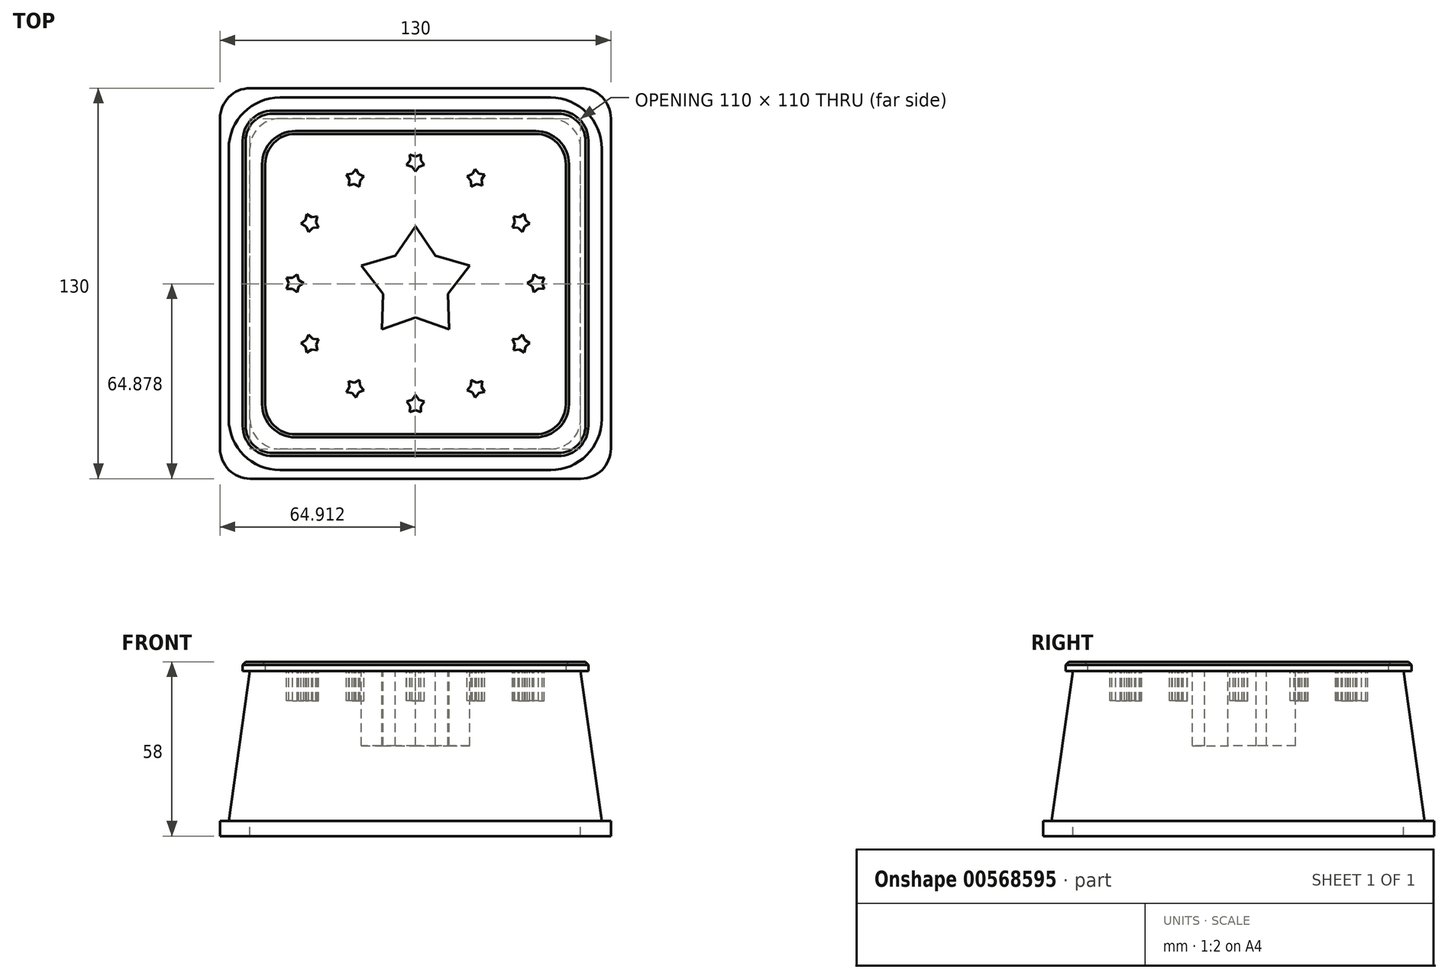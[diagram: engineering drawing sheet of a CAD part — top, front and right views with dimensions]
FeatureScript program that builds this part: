
annotation { "Feature Type Name" : "Feature", "Feature Type Description" : "" }
export const myFeature = defineFeature(function(context is Context, id is Id, definition is map)
    precondition{}
    {
        {
            var Q0;
            Q0=qCreatedBy(makeId("Top.planeOp"),FACE);
            var sketch = newSketch(context, id + "F0", { "sketchPlane" : qUnion([Q0])});
            skLineSegment(sketch, "E0", {"start": v(6.68, 9.2) * mm, "end": v(0, 18.96) * mm});
            skPoint(sketch, "E1.middle", {"position": v(0, 0) * mm});
            skPoint(sketch, "E2.visualSharp", {"position": v(-40, 40) * mm});
            skPoint(sketch, "E3.visualSharp", {"position": v(40, 40) * mm});
            skPoint(sketch, "E4.visualSharp", {"position": v(40, -40) * mm});
            skPoint(sketch, "E5.visualSharp", {"position": v(-40, -40) * mm});
            skLineSegment(sketch, "E6.bottom", {"start": v(40, -50.28) * mm, "end": v(-40, -50.28) * mm});
            skLineSegment(sketch, "E6.top", {"start": v(40, 49.72) * mm, "end": v(-40, 49.72) * mm});
            skLineSegment(sketch, "E6.left", {"start": v(50, -40.28) * mm, "end": v(50, 39.72) * mm});
            skLineSegment(sketch, "E6.right", {"start": v(-50, -40.28) * mm, "end": v(-50, 39.72) * mm});
            skArc(sketch, "E7.filletArc", {"start": v(-40, 49.72) * mm, "mid": v(-47.06, 46.79) * mm, "end": v(-50, 39.72) * mm});
            skArc(sketch, "E8.filletArc", {"start": v(50, 39.72) * mm, "mid": v(47.08, 46.79) * mm, "end": v(40, 49.72) * mm});
            skArc(sketch, "E9.filletArc", {"start": v(40, -50.28) * mm, "mid": v(47.08, -47.35) * mm, "end": v(50, -40.28) * mm});
            skArc(sketch, "E10.filletArc", {"start": v(-50, -40.28) * mm, "mid": v(-47.06, -47.35) * mm, "end": v(-40, -50.28) * mm});
            skLineSegment(sketch, "E11.bottom", {"start": v(44.91, -55.17) * mm, "end": v(-45.09, -55.17) * mm});
            skLineSegment(sketch, "E11.top", {"start": v(44.91, 54.83) * mm, "end": v(-45.09, 54.83) * mm});
            skLineSegment(sketch, "E11.left", {"start": v(54.91, -45.17) * mm, "end": v(54.91, 44.83) * mm});
            skLineSegment(sketch, "E11.right", {"start": v(-55.09, -45.17) * mm, "end": v(-55.09, 44.83) * mm});
            skArc(sketch, "E12.filletArc", {"start": v(-45.09, 54.83) * mm, "mid": v(-52.16, 51.9) * mm, "end": v(-55.09, 44.83) * mm});
            skArc(sketch, "E13.filletArc", {"start": v(54.91, 44.83) * mm, "mid": v(51.98, 51.9) * mm, "end": v(44.91, 54.83) * mm});
            skArc(sketch, "E14.filletArc", {"start": v(44.91, -55.17) * mm, "mid": v(51.98, -52.24) * mm, "end": v(54.91, -45.17) * mm});
            skArc(sketch, "E15.filletArc", {"start": v(-55.09, -45.17) * mm, "mid": v(-52.16, -52.24) * mm, "end": v(-45.09, -55.17) * mm});
            skLineSegment(sketch, "E16.bottom", {"start": v(47.51, -57.5) * mm, "end": v(-47.49, -57.5) * mm});
            skLineSegment(sketch, "E16.top", {"start": v(47.51, 57.5) * mm, "end": v(-47.49, 57.5) * mm});
            skLineSegment(sketch, "E16.left", {"start": v(57.51, -47.5) * mm, "end": v(57.51, 47.5) * mm});
            skLineSegment(sketch, "E16.right", {"start": v(-57.49, -47.5) * mm, "end": v(-57.49, 47.5) * mm});
            skArc(sketch, "E17.filletArc", {"start": v(-47.49, 57.5) * mm, "mid": v(-54.56, 54.56) * mm, "end": v(-57.49, 47.5) * mm});
            skArc(sketch, "E18.filletArc", {"start": v(57.51, 47.5) * mm, "mid": v(54.58, 54.56) * mm, "end": v(47.51, 57.5) * mm});
            skArc(sketch, "E19.filletArc", {"start": v(47.51, -57.5) * mm, "mid": v(54.58, -54.58) * mm, "end": v(57.51, -47.5) * mm});
            skArc(sketch, "E20.filletArc", {"start": v(-57.49, -47.5) * mm, "mid": v(-54.56, -54.58) * mm, "end": v(-47.49, -57.5) * mm});
            skLineSegment(sketch, "E21.bottom", {"start": v(55, -65.05) * mm, "end": v(-55, -65.05) * mm});
            skLineSegment(sketch, "E21.top", {"start": v(55, 64.95) * mm, "end": v(-55, 64.95) * mm});
            skLineSegment(sketch, "E21.left", {"start": v(65, -55.05) * mm, "end": v(65, 54.95) * mm});
            skLineSegment(sketch, "E21.right", {"start": v(-65, -55.05) * mm, "end": v(-65, 54.95) * mm});
            skArc(sketch, "E22.filletArc", {"start": v(-55, 64.95) * mm, "mid": v(-62.07, 62.02) * mm, "end": v(-65, 54.95) * mm});
            skArc(sketch, "E23.filletArc", {"start": v(65, 54.95) * mm, "mid": v(62.07, 62.02) * mm, "end": v(55, 64.95) * mm});
            skArc(sketch, "E24.filletArc", {"start": v(55, -65.05) * mm, "mid": v(62.07, -62.12) * mm, "end": v(65, -55.05) * mm});
            skArc(sketch, "E25.filletArc", {"start": v(-65, -55.05) * mm, "mid": v(-62.07, -62.12) * mm, "end": v(-55, -65.05) * mm});
            skLineSegment(sketch, "E26", {"start": v(-18.04, 5.85) * mm, "end": v(-10.83, -3.53) * mm});
            skLineSegment(sketch, "E27", {"start": v(-10.83, -3.53) * mm, "end": v(-11.15, -15.35) * mm});
            skLineSegment(sketch, "E28", {"start": v(-11.15, -15.35) * mm, "end": v(0, -11.39) * mm});
            skLineSegment(sketch, "E29", {"start": v(0, -11.39) * mm, "end": v(11.13, -15.35) * mm});
            skLineSegment(sketch, "E30", {"start": v(11.13, -15.35) * mm, "end": v(10.8, -3.53) * mm});
            skLineSegment(sketch, "E31", {"start": v(10.8, -3.53) * mm, "end": v(18.02, 5.85) * mm});
            skLineSegment(sketch, "E32", {"start": v(18.02, 5.85) * mm, "end": v(6.68, 9.19) * mm});
            skLineSegment(sketch, "E33", {"start": v(6.68, 9.19) * mm, "end": v(0, 18.94) * mm});
            skLineSegment(sketch, "E34", {"start": v(0, 18.94) * mm, "end": v(-6.7, 9.19) * mm});
            skLineSegment(sketch, "E35", {"start": v(-6.7, 9.19) * mm, "end": v(-18.04, 5.85) * mm});
            skPoint(sketch, "E36.middle", {"position": v(0, -0.01) * mm});
            skLineSegment(sketch, "E37", {"start": v(0, -42.21) * mm, "end": v(1.85, -42.87) * mm});
            skLineSegment(sketch, "E38", {"start": v(1.8, -40.92) * mm, "end": v(2.98, -39.37) * mm});
            skLineSegment(sketch, "E39", {"start": v(1.11, -38.82) * mm, "end": v(0, -37.21) * mm});
            skLineSegment(sketch, "E40", {"start": v(-1.1, -38.82) * mm, "end": v(-2.96, -39.37) * mm});
            skPoint(sketch, "E41.middle", {"position": v(0, -40.34) * mm});
            skLineSegment(sketch, "E42", {"start": v(-1.78, -40.92) * mm, "end": v(-1.83, -42.87) * mm});
            skLineSegment(sketch, "E43", {"start": v(1.8, -40.92) * mm, "end": v(1.85, -42.87) * mm});
            skLineSegment(sketch, "E44", {"start": v(0, -42.21) * mm, "end": v(-1.83, -42.87) * mm});
            skLineSegment(sketch, "E45", {"start": v(-1.78, -40.92) * mm, "end": v(-2.96, -39.37) * mm});
            skLineSegment(sketch, "E46", {"start": v(-1.1, -38.82) * mm, "end": v(0, -37.21) * mm});
            skLineSegment(sketch, "E47", {"start": v(1.11, -38.82) * mm, "end": v(2.98, -39.37) * mm});
            skLineSegment(sketch, "E48.1.0", {"start": v(18.92, -36.33) * mm, "end": v(17.12, -35.58) * mm});
            skLineSegment(sketch, "E48.1.1", {"start": v(18.92, -36.33) * mm, "end": v(19.85, -38.04) * mm});
            skLineSegment(sketch, "E48.1.2", {"start": v(21.11, -36.55) * mm, "end": v(19.85, -38.04) * mm});
            skLineSegment(sketch, "E48.1.3", {"start": v(22.01, -34.54) * mm, "end": v(22.27, -32.6) * mm});
            skLineSegment(sketch, "E48.1.4", {"start": v(20.37, -33.07) * mm, "end": v(22.27, -32.6) * mm});
            skPoint(sketch, "E48.1.5", {"position": v(20.18, -34.93) * mm});
            skLineSegment(sketch, "E48.1.6", {"start": v(18.46, -34.17) * mm, "end": v(17.12, -35.58) * mm});
            skLineSegment(sketch, "E48.1.7", {"start": v(22.01, -34.54) * mm, "end": v(23.03, -36.2) * mm});
            skLineSegment(sketch, "E48.1.8", {"start": v(18.46, -34.17) * mm, "end": v(18.61, -32.22) * mm});
            skLineSegment(sketch, "E48.1.9", {"start": v(20.37, -33.07) * mm, "end": v(18.61, -32.22) * mm});
            skLineSegment(sketch, "E48.1.10", {"start": v(21.11, -36.55) * mm, "end": v(23.03, -36.2) * mm});
            skPoint(sketch, "E48.1.11", {"position": v(20.18, -34.93) * mm});
            skLineSegment(sketch, "E48.2.0", {"start": v(34.55, -22) * mm, "end": v(32.62, -22.25) * mm});
            skLineSegment(sketch, "E48.2.1", {"start": v(34.55, -22) * mm, "end": v(36.21, -23.02) * mm});
            skLineSegment(sketch, "E48.2.2", {"start": v(36.56, -21.1) * mm, "end": v(36.21, -23.02) * mm});
            skLineSegment(sketch, "E48.2.3", {"start": v(36.33, -18.9) * mm, "end": v(35.59, -17.1) * mm});
            skLineSegment(sketch, "E48.2.4", {"start": v(34.18, -18.45) * mm, "end": v(35.59, -17.1) * mm});
            skPoint(sketch, "E48.2.5", {"position": v(34.94, -20.16) * mm});
            skLineSegment(sketch, "E48.2.6", {"start": v(33.07, -20.36) * mm, "end": v(32.62, -22.25) * mm});
            skLineSegment(sketch, "E48.2.7", {"start": v(36.33, -18.9) * mm, "end": v(38.05, -19.84) * mm});
            skLineSegment(sketch, "E48.2.8", {"start": v(33.07, -20.36) * mm, "end": v(32.23, -18.6) * mm});
            skLineSegment(sketch, "E48.2.9", {"start": v(34.18, -18.45) * mm, "end": v(32.23, -18.6) * mm});
            skLineSegment(sketch, "E48.2.10", {"start": v(36.56, -21.1) * mm, "end": v(38.05, -19.84) * mm});
            skPoint(sketch, "E48.2.11", {"position": v(34.94, -20.16) * mm});
            skLineSegment(sketch, "E48.3.0", {"start": v(40.92, -1.78) * mm, "end": v(39.37, -2.96) * mm});
            skLineSegment(sketch, "E48.3.1", {"start": v(40.92, -1.78) * mm, "end": v(42.87, -1.83) * mm});
            skLineSegment(sketch, "E48.3.2", {"start": v(42.21, 0) * mm, "end": v(42.87, -1.83) * mm});
            skLineSegment(sketch, "E48.3.3", {"start": v(40.92, 1.8) * mm, "end": v(39.37, 2.98) * mm});
            skLineSegment(sketch, "E48.3.4", {"start": v(38.82, 1.11) * mm, "end": v(39.37, 2.98) * mm});
            skPoint(sketch, "E48.3.5", {"position": v(40.34, 0) * mm});
            skLineSegment(sketch, "E48.3.6", {"start": v(38.82, -1.1) * mm, "end": v(39.37, -2.96) * mm});
            skLineSegment(sketch, "E48.3.7", {"start": v(40.92, 1.8) * mm, "end": v(42.87, 1.85) * mm});
            skLineSegment(sketch, "E48.3.8", {"start": v(38.82, -1.1) * mm, "end": v(37.21, 0) * mm});
            skLineSegment(sketch, "E48.3.9", {"start": v(38.82, 1.11) * mm, "end": v(37.21, 0) * mm});
            skLineSegment(sketch, "E48.3.10", {"start": v(42.21, 0) * mm, "end": v(42.87, 1.85) * mm});
            skPoint(sketch, "E48.3.11", {"position": v(40.34, 0) * mm});
            skLineSegment(sketch, "E48.4.0", {"start": v(36.33, 18.92) * mm, "end": v(35.58, 17.12) * mm});
            skLineSegment(sketch, "E48.4.1", {"start": v(36.33, 18.92) * mm, "end": v(38.04, 19.85) * mm});
            skLineSegment(sketch, "E48.4.2", {"start": v(36.55, 21.11) * mm, "end": v(38.04, 19.85) * mm});
            skLineSegment(sketch, "E48.4.3", {"start": v(34.54, 22.01) * mm, "end": v(32.6, 22.27) * mm});
            skLineSegment(sketch, "E48.4.4", {"start": v(33.07, 20.37) * mm, "end": v(32.6, 22.27) * mm});
            skPoint(sketch, "E48.4.5", {"position": v(34.93, 20.18) * mm});
            skLineSegment(sketch, "E48.4.6", {"start": v(34.17, 18.46) * mm, "end": v(35.58, 17.12) * mm});
            skLineSegment(sketch, "E48.4.7", {"start": v(34.54, 22.01) * mm, "end": v(36.2, 23.03) * mm});
            skLineSegment(sketch, "E48.4.8", {"start": v(34.17, 18.46) * mm, "end": v(32.22, 18.61) * mm});
            skLineSegment(sketch, "E48.4.9", {"start": v(33.07, 20.37) * mm, "end": v(32.22, 18.61) * mm});
            skLineSegment(sketch, "E48.4.10", {"start": v(36.55, 21.11) * mm, "end": v(36.2, 23.03) * mm});
            skPoint(sketch, "E48.4.11", {"position": v(34.93, 20.18) * mm});
            skLineSegment(sketch, "E48.5.0", {"start": v(22, 34.55) * mm, "end": v(22.25, 32.62) * mm});
            skLineSegment(sketch, "E48.5.1", {"start": v(22, 34.55) * mm, "end": v(23.02, 36.21) * mm});
            skLineSegment(sketch, "E48.5.2", {"start": v(21.1, 36.56) * mm, "end": v(23.02, 36.21) * mm});
            skLineSegment(sketch, "E48.5.3", {"start": v(18.9, 36.33) * mm, "end": v(17.1, 35.59) * mm});
            skLineSegment(sketch, "E48.5.4", {"start": v(18.45, 34.18) * mm, "end": v(17.1, 35.59) * mm});
            skPoint(sketch, "E48.5.5", {"position": v(20.16, 34.94) * mm});
            skLineSegment(sketch, "E48.5.6", {"start": v(20.36, 33.07) * mm, "end": v(22.25, 32.62) * mm});
            skLineSegment(sketch, "E48.5.7", {"start": v(18.9, 36.33) * mm, "end": v(19.84, 38.05) * mm});
            skLineSegment(sketch, "E48.5.8", {"start": v(20.36, 33.07) * mm, "end": v(18.6, 32.23) * mm});
            skLineSegment(sketch, "E48.5.9", {"start": v(18.45, 34.18) * mm, "end": v(18.6, 32.23) * mm});
            skLineSegment(sketch, "E48.5.10", {"start": v(21.1, 36.56) * mm, "end": v(19.84, 38.05) * mm});
            skPoint(sketch, "E48.5.11", {"position": v(20.16, 34.94) * mm});
            skLineSegment(sketch, "E48.6.0", {"start": v(1.78, 40.92) * mm, "end": v(2.96, 39.37) * mm});
            skLineSegment(sketch, "E48.6.1", {"start": v(1.78, 40.92) * mm, "end": v(1.83, 42.87) * mm});
            skLineSegment(sketch, "E48.6.2", {"start": v(0, 42.21) * mm, "end": v(1.83, 42.87) * mm});
            skLineSegment(sketch, "E48.6.3", {"start": v(-1.8, 40.92) * mm, "end": v(-2.98, 39.37) * mm});
            skLineSegment(sketch, "E48.6.4", {"start": v(-1.11, 38.82) * mm, "end": v(-2.98, 39.37) * mm});
            skPoint(sketch, "E48.6.5", {"position": v(0, 40.34) * mm});
            skLineSegment(sketch, "E48.6.6", {"start": v(1.1, 38.82) * mm, "end": v(2.96, 39.37) * mm});
            skLineSegment(sketch, "E48.6.7", {"start": v(-1.8, 40.92) * mm, "end": v(-1.85, 42.87) * mm});
            skLineSegment(sketch, "E48.6.8", {"start": v(1.1, 38.82) * mm, "end": v(0, 37.21) * mm});
            skLineSegment(sketch, "E48.6.9", {"start": v(-1.11, 38.82) * mm, "end": v(0, 37.21) * mm});
            skLineSegment(sketch, "E48.6.10", {"start": v(0, 42.21) * mm, "end": v(-1.85, 42.87) * mm});
            skPoint(sketch, "E48.6.11", {"position": v(0, 40.34) * mm});
            skLineSegment(sketch, "E48.7.0", {"start": v(-18.92, 36.33) * mm, "end": v(-17.12, 35.58) * mm});
            skLineSegment(sketch, "E48.7.1", {"start": v(-18.92, 36.33) * mm, "end": v(-19.85, 38.04) * mm});
            skLineSegment(sketch, "E48.7.2", {"start": v(-21.11, 36.55) * mm, "end": v(-19.85, 38.04) * mm});
            skLineSegment(sketch, "E48.7.3", {"start": v(-22.01, 34.54) * mm, "end": v(-22.27, 32.6) * mm});
            skLineSegment(sketch, "E48.7.4", {"start": v(-20.37, 33.07) * mm, "end": v(-22.27, 32.6) * mm});
            skPoint(sketch, "E48.7.5", {"position": v(-20.18, 34.93) * mm});
            skLineSegment(sketch, "E48.7.6", {"start": v(-18.46, 34.17) * mm, "end": v(-17.12, 35.58) * mm});
            skLineSegment(sketch, "E48.7.7", {"start": v(-22.01, 34.54) * mm, "end": v(-23.03, 36.2) * mm});
            skLineSegment(sketch, "E48.7.8", {"start": v(-18.46, 34.17) * mm, "end": v(-18.61, 32.22) * mm});
            skLineSegment(sketch, "E48.7.9", {"start": v(-20.37, 33.07) * mm, "end": v(-18.61, 32.22) * mm});
            skLineSegment(sketch, "E48.7.10", {"start": v(-21.11, 36.55) * mm, "end": v(-23.03, 36.2) * mm});
            skPoint(sketch, "E48.7.11", {"position": v(-20.18, 34.93) * mm});
            skLineSegment(sketch, "E48.8.0", {"start": v(-34.55, 22) * mm, "end": v(-32.62, 22.25) * mm});
            skLineSegment(sketch, "E48.8.1", {"start": v(-34.55, 22) * mm, "end": v(-36.21, 23.02) * mm});
            skLineSegment(sketch, "E48.8.2", {"start": v(-36.56, 21.1) * mm, "end": v(-36.21, 23.02) * mm});
            skLineSegment(sketch, "E48.8.3", {"start": v(-36.33, 18.9) * mm, "end": v(-35.59, 17.1) * mm});
            skLineSegment(sketch, "E48.8.4", {"start": v(-34.18, 18.45) * mm, "end": v(-35.59, 17.1) * mm});
            skPoint(sketch, "E48.8.5", {"position": v(-34.94, 20.16) * mm});
            skLineSegment(sketch, "E48.8.6", {"start": v(-33.07, 20.36) * mm, "end": v(-32.62, 22.25) * mm});
            skLineSegment(sketch, "E48.8.7", {"start": v(-36.33, 18.9) * mm, "end": v(-38.05, 19.84) * mm});
            skLineSegment(sketch, "E48.8.8", {"start": v(-33.07, 20.36) * mm, "end": v(-32.23, 18.6) * mm});
            skLineSegment(sketch, "E48.8.9", {"start": v(-34.18, 18.45) * mm, "end": v(-32.23, 18.6) * mm});
            skLineSegment(sketch, "E48.8.10", {"start": v(-36.56, 21.1) * mm, "end": v(-38.05, 19.84) * mm});
            skPoint(sketch, "E48.8.11", {"position": v(-34.94, 20.16) * mm});
            skLineSegment(sketch, "E48.9.0", {"start": v(-40.92, 1.78) * mm, "end": v(-39.37, 2.96) * mm});
            skLineSegment(sketch, "E48.9.1", {"start": v(-40.92, 1.78) * mm, "end": v(-42.87, 1.83) * mm});
            skLineSegment(sketch, "E48.9.2", {"start": v(-42.21, 0) * mm, "end": v(-42.87, 1.83) * mm});
            skLineSegment(sketch, "E48.9.3", {"start": v(-40.92, -1.8) * mm, "end": v(-39.37, -2.98) * mm});
            skLineSegment(sketch, "E48.9.4", {"start": v(-38.82, -1.11) * mm, "end": v(-39.37, -2.98) * mm});
            skPoint(sketch, "E48.9.5", {"position": v(-40.34, 0) * mm});
            skLineSegment(sketch, "E48.9.6", {"start": v(-38.82, 1.1) * mm, "end": v(-39.37, 2.96) * mm});
            skLineSegment(sketch, "E48.9.7", {"start": v(-40.92, -1.8) * mm, "end": v(-42.87, -1.85) * mm});
            skLineSegment(sketch, "E48.9.8", {"start": v(-38.82, 1.1) * mm, "end": v(-37.21, 0) * mm});
            skLineSegment(sketch, "E48.9.9", {"start": v(-38.82, -1.11) * mm, "end": v(-37.21, 0) * mm});
            skLineSegment(sketch, "E48.9.10", {"start": v(-42.21, 0) * mm, "end": v(-42.87, -1.85) * mm});
            skPoint(sketch, "E48.9.11", {"position": v(-40.34, 0) * mm});
            skLineSegment(sketch, "E48.10.0", {"start": v(-36.33, -18.92) * mm, "end": v(-35.58, -17.12) * mm});
            skLineSegment(sketch, "E48.10.1", {"start": v(-36.33, -18.92) * mm, "end": v(-38.04, -19.85) * mm});
            skLineSegment(sketch, "E48.10.2", {"start": v(-36.55, -21.11) * mm, "end": v(-38.04, -19.85) * mm});
            skLineSegment(sketch, "E48.10.3", {"start": v(-34.54, -22.01) * mm, "end": v(-32.6, -22.27) * mm});
            skLineSegment(sketch, "E48.10.4", {"start": v(-33.07, -20.37) * mm, "end": v(-32.6, -22.27) * mm});
            skPoint(sketch, "E48.10.5", {"position": v(-34.93, -20.18) * mm});
            skLineSegment(sketch, "E48.10.6", {"start": v(-34.17, -18.46) * mm, "end": v(-35.58, -17.12) * mm});
            skLineSegment(sketch, "E48.10.7", {"start": v(-34.54, -22.01) * mm, "end": v(-36.2, -23.03) * mm});
            skLineSegment(sketch, "E48.10.8", {"start": v(-34.17, -18.46) * mm, "end": v(-32.22, -18.61) * mm});
            skLineSegment(sketch, "E48.10.9", {"start": v(-33.07, -20.37) * mm, "end": v(-32.22, -18.61) * mm});
            skLineSegment(sketch, "E48.10.10", {"start": v(-36.55, -21.11) * mm, "end": v(-36.2, -23.03) * mm});
            skPoint(sketch, "E48.10.11", {"position": v(-34.93, -20.18) * mm});
            skLineSegment(sketch, "E48.11.0", {"start": v(-22, -34.55) * mm, "end": v(-22.25, -32.62) * mm});
            skLineSegment(sketch, "E48.11.1", {"start": v(-22, -34.55) * mm, "end": v(-23.02, -36.21) * mm});
            skLineSegment(sketch, "E48.11.2", {"start": v(-21.1, -36.56) * mm, "end": v(-23.02, -36.21) * mm});
            skLineSegment(sketch, "E48.11.3", {"start": v(-18.9, -36.33) * mm, "end": v(-17.1, -35.59) * mm});
            skLineSegment(sketch, "E48.11.4", {"start": v(-18.45, -34.18) * mm, "end": v(-17.1, -35.59) * mm});
            skPoint(sketch, "E48.11.5", {"position": v(-20.16, -34.94) * mm});
            skLineSegment(sketch, "E48.11.6", {"start": v(-20.36, -33.07) * mm, "end": v(-22.25, -32.62) * mm});
            skLineSegment(sketch, "E48.11.7", {"start": v(-18.9, -36.33) * mm, "end": v(-19.84, -38.05) * mm});
            skLineSegment(sketch, "E48.11.8", {"start": v(-20.36, -33.07) * mm, "end": v(-18.6, -32.23) * mm});
            skLineSegment(sketch, "E48.11.9", {"start": v(-18.45, -34.18) * mm, "end": v(-18.6, -32.23) * mm});
            skLineSegment(sketch, "E48.11.10", {"start": v(-21.1, -36.56) * mm, "end": v(-19.84, -38.05) * mm});
            skPoint(sketch, "E48.11.11", {"position": v(-20.16, -34.94) * mm});
            skSolve(sketch);
        }
        {
            var Q0;
            Q0=makeQuery(id+"F0.imprint","IMPRINT",FACE,{"disambiguationData":[TD([[makeQuery(id+"F0.imprint","IMPRINT",EDGE,{"derivedFrom":sQuery(id+"F0.wireOp",EDGE,"E6.bottom")}),-1.0]])]});
            extrude(context, id + "F1", {"entities" : qUnion([Q0]), "oppositeDirection" : true, "depth" : 50 * mm, "offsetDistance" : 25 * mm});
        }
        {
            var Q0;
            Q0=makeQuery(id+"F0.imprint","IMPRINT",FACE,{"disambiguationData":[TD([[makeQuery(id+"F0.imprint","IMPRINT",EDGE,{"derivedFrom":sQuery(id+"F0.wireOp",EDGE,"E6.bottom")}),1.0]])]});
            var Q1;
            Q1=makeQuery(id+"F0.imprint","IMPRINT",FACE,{"disambiguationData":[TD([[makeQuery(id+"F0.imprint","IMPRINT",EDGE,{"derivedFrom":sQuery(id+"F0.wireOp",EDGE,"E11.bottom")}),1.0]])]});
            extrude(context, id + "F2", {"entities" : qUnion([Q0, Q1]), "depth" : 3 * mm, "offsetDistance" : 25 * mm});
        }
        {
            var Q0;
            Q0=makeQuery(id+"F2.opExtrude","CAP_FACE",FACE,{"disambiguationData":[OSD([sQuery(id+"F0.wireOp",EDGE,"E6.bottom"),sQuery(id+"F0.wireOp",EDGE,"E6.top"),sQuery(id+"F0.wireOp",EDGE,"E6.left"),sQuery(id+"F0.wireOp",EDGE,"E6.right"),sQuery(id+"F0.wireOp",EDGE,"E7.filletArc"),sQuery(id+"F0.wireOp",EDGE,"E8.filletArc"),sQuery(id+"F0.wireOp",EDGE,"E9.filletArc"),sQuery(id+"F0.wireOp",EDGE,"E10.filletArc"),sQuery(id+"F0.wireOp",EDGE,"E16.bottom"),sQuery(id+"F0.wireOp",EDGE,"E16.top"),sQuery(id+"F0.wireOp",EDGE,"E16.left"),sQuery(id+"F0.wireOp",EDGE,"E16.right"),sQuery(id+"F0.wireOp",EDGE,"E17.filletArc"),sQuery(id+"F0.wireOp",EDGE,"E18.filletArc"),sQuery(id+"F0.wireOp",EDGE,"E19.filletArc"),sQuery(id+"F0.wireOp",EDGE,"E20.filletArc")])],"isStart":false});
            chamfer(context, id + "F3", {"entities" : qUnion([Q0]), "chamferType" : ChamferType.OFFSET_ANGLE, "width" : 1 * mm, "oppositeDirection" : false, "angle" : 45 * degree});
        }
        {
            var Q0;
            Q0=makeQuery(id+"F0.imprint","IMPRINT",FACE,{"disambiguationData":[TD([[makeQuery(id+"F0.imprint","IMPRINT",EDGE,{"derivedFrom":sQuery(id+"F0.wireOp",EDGE,"E11.bottom")}),1.0]])]});
            var Q1;
            Q1=makeQuery(id+"F0.imprint","IMPRINT",FACE,{"disambiguationData":[TD([[makeQuery(id+"F0.imprint","IMPRINT",EDGE,{"derivedFrom":sQuery(id+"F0.wireOp",EDGE,"E16.bottom")}),1.0]])]});
            extrude(context, id + "F4", {"entities" : qUnion([Q0, Q1]), "oppositeDirection" : true, "depth" : 55 * mm, "offsetDistance" : 25 * mm, "hasSecondDirection" : true, "secondDirectionOppositeDirection" : true, "secondDirectionDepth" : 50 * mm});
        }
        {
            var Q0;
            Q0=makeQuery(id+"F0.imprint","IMPRINT",FACE,{"disambiguationData":[TD([[makeQuery(id+"F0.imprint","IMPRINT",EDGE,{"derivedFrom":sQuery(id+"F0.wireOp",EDGE,"E6.bottom")}),1.0]])]});
            extrude(context, id + "F5", {"entities" : qUnion([Q0]), "operationType" : NewBodyOperationType.ADD, "oppositeDirection" : true, "depth" : 50 * mm, "offsetDistance" : 25 * mm, "hasDraft" : true, "draftAngle" : 8 * degree});
        }
        {
            var Q0;
            Q0=makeQuery(id+"F0.imprint","IMPRINT",FACE,{"disambiguationData":[TD([[makeQuery(id+"F0.imprint","IMPRINT",EDGE,{"derivedFrom":sQuery(id+"F0.wireOp",EDGE,"E26")}),1.0]])]});
            extrude(context, id + "F6", {"entities" : qUnion([Q0]), "operationType" : NewBodyOperationType.ADD, "oppositeDirection" : true, "depth" : 50 * mm, "offsetDistance" : 25 * mm, "hasSecondDirection" : true, "secondDirectionOppositeDirection" : true, "secondDirectionDepth" : 25 * mm});
        }
        {
            var Q0;
            Q0=makeQuery(id+"F0.imprint","IMPRINT",FACE,{"disambiguationData":[TD([[makeQuery(id+"F0.imprint","IMPRINT",EDGE,{"derivedFrom":sQuery(id+"F0.wireOp",EDGE,"E48.2.0")}),-1.0]])]});
            var Q1;
            Q1=makeQuery(id+"F0.imprint","IMPRINT",FACE,{"disambiguationData":[TD([[makeQuery(id+"F0.imprint","IMPRINT",EDGE,{"derivedFrom":sQuery(id+"F0.wireOp",EDGE,"E48.3.0")}),-1.0]])]});
            var Q2;
            Q2=makeQuery(id+"F0.imprint","IMPRINT",FACE,{"disambiguationData":[TD([[makeQuery(id+"F0.imprint","IMPRINT",EDGE,{"derivedFrom":sQuery(id+"F0.wireOp",EDGE,"E48.1.0")}),-1.0]])]});
            var Q3;
            Q3=makeQuery(id+"F0.imprint","IMPRINT",FACE,{"disambiguationData":[TD([[makeQuery(id+"F0.imprint","IMPRINT",EDGE,{"derivedFrom":sQuery(id+"F0.wireOp",EDGE,"E37")}),1.0]])]});
            var Q4;
            Q4=makeQuery(id+"F0.imprint","IMPRINT",FACE,{"disambiguationData":[TD([[makeQuery(id+"F0.imprint","IMPRINT",EDGE,{"derivedFrom":sQuery(id+"F0.wireOp",EDGE,"E48.11.0")}),-1.0]])]});
            var Q5;
            Q5=makeQuery(id+"F0.imprint","IMPRINT",FACE,{"disambiguationData":[TD([[makeQuery(id+"F0.imprint","IMPRINT",EDGE,{"derivedFrom":sQuery(id+"F0.wireOp",EDGE,"E48.10.0")}),-1.0]])]});
            var Q6;
            Q6=makeQuery(id+"F0.imprint","IMPRINT",FACE,{"disambiguationData":[TD([[makeQuery(id+"F0.imprint","IMPRINT",EDGE,{"derivedFrom":sQuery(id+"F0.wireOp",EDGE,"E48.9.0")}),-1.0]])]});
            var Q7;
            Q7=makeQuery(id+"F0.imprint","IMPRINT",FACE,{"disambiguationData":[TD([[makeQuery(id+"F0.imprint","IMPRINT",EDGE,{"derivedFrom":sQuery(id+"F0.wireOp",EDGE,"E48.7.0")}),-1.0]])]});
            var Q8;
            Q8=makeQuery(id+"F0.imprint","IMPRINT",FACE,{"disambiguationData":[TD([[makeQuery(id+"F0.imprint","IMPRINT",EDGE,{"derivedFrom":sQuery(id+"F0.wireOp",EDGE,"E48.6.0")}),-1.0]])]});
            var Q9;
            Q9=makeQuery(id+"F0.imprint","IMPRINT",FACE,{"disambiguationData":[TD([[makeQuery(id+"F0.imprint","IMPRINT",EDGE,{"derivedFrom":sQuery(id+"F0.wireOp",EDGE,"E48.5.0")}),-1.0]])]});
            var Q10;
            Q10=makeQuery(id+"F0.imprint","IMPRINT",FACE,{"disambiguationData":[TD([[makeQuery(id+"F0.imprint","IMPRINT",EDGE,{"derivedFrom":sQuery(id+"F0.wireOp",EDGE,"E48.4.0")}),-1.0]])]});
            var Q11;
            Q11=makeQuery(id+"F0.imprint","IMPRINT",FACE,{"disambiguationData":[TD([[makeQuery(id+"F0.imprint","IMPRINT",EDGE,{"derivedFrom":sQuery(id+"F0.wireOp",EDGE,"E48.8.0")}),-1.0]])]});
            extrude(context, id + "F7", {"entities" : qUnion([Q0, Q1, Q2, Q3, Q4, Q5, Q6, Q7, Q8, Q9, Q10, Q11]), "operationType" : NewBodyOperationType.ADD, "oppositeDirection" : true, "depth" : 50 * mm, "offsetDistance" : 25 * mm, "hasSecondDirection" : true, "secondDirectionOppositeDirection" : true, "secondDirectionDepth" : 10 * mm});
        }
    });
